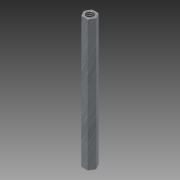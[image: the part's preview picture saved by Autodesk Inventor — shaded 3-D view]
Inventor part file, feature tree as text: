
AUTODESK INVENTOR PART (.ipt)
format: ipt  version: 2011 (Build 150239000, 239)  size: 114,176 bytes
history: native  units: in
note: dims shown in document units (in); Inventor stores cm internally (conversion verified against a paired STEP export)
features: thread x2, other x1, imported_body x1
ambient origin geometry x8: Origin, YZ Plane, XZ Plane, XY Plane, X Axis, Y Axis, Z Axis, Center Point
feature tree (4):
  parser-record x1  (decoder bookkeeping rows leaked as tree rows — omitted from the tree; the rows remain in map.json)
  imported_body  "Base1"
  thread  "Thread1"  [1 undecoded]
  thread  "Thread2"  [1 undecoded]
note: 2 required parameter values undecoded (feature->parameter linkage not recoverable at this tier; creation-order binding heuristic only, values carry confidence <= 0.55)
